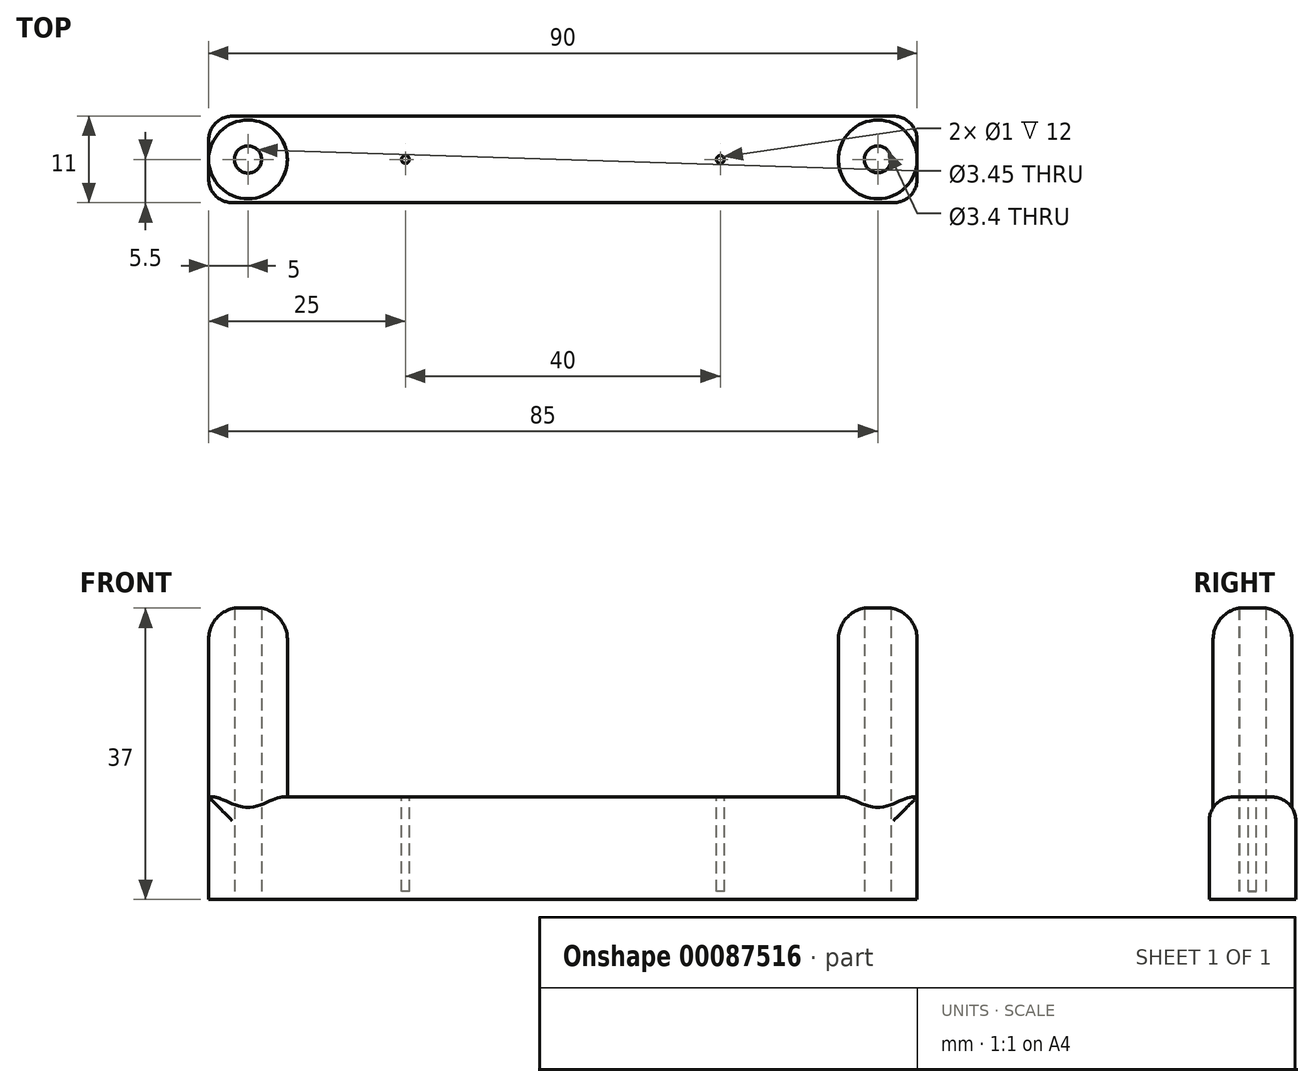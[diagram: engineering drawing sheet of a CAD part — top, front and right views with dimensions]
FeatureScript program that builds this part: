
annotation { "Feature Type Name" : "Feature", "Feature Type Description" : "" }
export const myFeature = defineFeature(function(context is Context, id is Id, definition is map)
    precondition{}
    {
        {
            var Q0;
            Q0=qCreatedBy(makeId("Top.planeOp"),FACE);
            var sketch = newSketch(context, id + "F0", { "sketchPlane" : qUnion([Q0])});
            skLineSegment(sketch, "E0.bottom", {"start": v(45, -5.5) * mm, "end": v(-45, -5.5) * mm});
            skLineSegment(sketch, "E0.top", {"start": v(45, 5.5) * mm, "end": v(-45, 5.5) * mm});
            skLineSegment(sketch, "E0.left", {"start": v(45, -5.5) * mm, "end": v(45, 5.5) * mm});
            skLineSegment(sketch, "E0.right", {"start": v(-45, -5.5) * mm, "end": v(-45, 5.5) * mm});
            skCircle(sketch, "E1", {"center": v(-40, 0) * mm, "radius": 1.73 * mm});
            skCircle(sketch, "E2", {"center": v(40, 0) * mm, "radius": 1.7 * mm});
            skSolve(sketch);
        }
        {
            var Q0;
            Q0=makeQuery(id+"F0.imprint","IMPRINT",FACE,{"disambiguationData":[TD([[makeQuery(id+"F0.imprint","IMPRINT",EDGE,{"derivedFrom":sQuery(id+"F0.wireOp",EDGE,"E0.bottom")}),-1.0]])]});
            var Q1;
            Q1=makeQuery(id+"F0.imprint","IMPRINT",FACE,{"disambiguationData":[TD([[makeQuery(id+"F0.imprint","IMPRINT",EDGE,{"derivedFrom":sQuery(id+"F0.wireOp",EDGE,"79vgDt6U-RJey-WxaV-HGEM-l305grDqS5GU")}),1.0]])]});
            extrude(context, id + "F1", {"entities" : qUnion([Q0, Q1]), "depth" : 13 * mm});
        }
        {
            var Q0;
            Q0=makeQuery(id+"F1.opExtrude","CAP_FACE",FACE,{"disambiguationData":[OSD([sQuery(id+"F0.wireOp",EDGE,"E0.bottom"),sQuery(id+"F0.wireOp",EDGE,"E0.top"),sQuery(id+"F0.wireOp",EDGE,"E0.left"),sQuery(id+"F0.wireOp",EDGE,"E0.right"),sQuery(id+"F0.wireOp",EDGE,"E1"),sQuery(id+"F0.wireOp",EDGE,"E2")])],"isStart":false});
            var sketch = newSketch(context, id + "F2", { "sketchPlane" : qUnion([Q0])});
            skCircle(sketch, "E3", {"center": v(40, 0) * mm, "radius": 5 * mm});
            skSolve(sketch);
        }
        {
            var Q0;
            Q0=makeQuery(id+"F2.imprint","IMPRINT",FACE,{"disambiguationData":[TD([[makeQuery(id+"F2.imprint","IMPRINT",EDGE,{"derivedFrom":sQuery(id+"F2.wireOp",EDGE,"E3")}),1.0]])]});
            extrude(context, id + "F3", {"entities" : qUnion([Q0]), "operationType" : NewBodyOperationType.ADD, "depth" : 24 * mm});
        }
        {
            var Q0;
            Q0=makeQuery(id+"F1.opExtrude","CAP_FACE",FACE,{"disambiguationData":[OSD([sQuery(id+"F0.wireOp",EDGE,"E0.bottom"),sQuery(id+"F0.wireOp",EDGE,"E0.top"),sQuery(id+"F0.wireOp",EDGE,"E0.left"),sQuery(id+"F0.wireOp",EDGE,"E0.right"),sQuery(id+"F0.wireOp",EDGE,"E1"),sQuery(id+"F0.wireOp",EDGE,"E2")])],"isStart":false});
            var sketch = newSketch(context, id + "F4", { "sketchPlane" : qUnion([Q0])});
            skCircle(sketch, "E4", {"center": v(-40, 0) * mm, "radius": 5 * mm});
            skSolve(sketch);
        }
        {
            var Q0;
            Q0=makeQuery(id+"F4.imprint","IMPRINT",FACE,{"disambiguationData":[TD([[makeQuery(id+"F4.imprint","IMPRINT",EDGE,{"derivedFrom":sQuery(id+"F4.wireOp",EDGE,"E4")}),1.0]])]});
            extrude(context, id + "F5", {"entities" : qUnion([Q0]), "operationType" : NewBodyOperationType.ADD, "depth" : 24 * mm});
        }
        {
            var Q0;
            {var subQ2=sQuery(id+"F2.wireOp",EDGE,"E3");Q0=makeQuery(id+"F2.imprint","IMPRINT",FACE,{"disambiguationData":[TD([[makeQuery(id+"F2.imprint","IMPRINT",EDGE,{"derivedFrom":subQ2}),-1.0]])]});}
            var sketch = newSketch(context, id + "F6", { "sketchPlane" : qUnion([Q0])});
            skCircle(sketch, "E5", {"center": v(-20, 0) * mm, "radius": 0.5 * mm});
            skCircle(sketch, "E6", {"center": v(20, 0) * mm, "radius": 0.5 * mm});
            skSolve(sketch);
        }
        {
            var Q0;
            Q0=qSketchRegion(id+"F6",true);
            extrude(context, id + "F7", {"entities" : qUnion([Q0]), "operationType" : NewBodyOperationType.REMOVE, "oppositeDirection" : true, "depth" : 12 * mm});
        }
        {
            var Q0;
            Q0=makeQuery(id+"F1.opExtrude","CAP_EDGE",EDGE,{"disambiguationData":[OSD([sQuery(id+"F0.wireOp",EDGE,"E0.bottom")])],"isStart":false});
            var Q1;
            Q1=makeQuery(id+"F1.opExtrude","SWEPT_EDGE",EDGE,{"disambiguationData":[OSD([sQuery(id+"F0.wireOp",EDGE,"E0.bottom"),sQuery(id+"F0.wireOp",EDGE,"E0.right")])]});
            var Q2;
            Q2=makeQuery(id+"F1.opExtrude","SWEPT_EDGE",EDGE,{"disambiguationData":[OSD([sQuery(id+"F0.wireOp",EDGE,"E0.top"),sQuery(id+"F0.wireOp",EDGE,"E0.right")])]});
            var Q3;
            Q3=makeQuery(id+"F1.opExtrude","CAP_EDGE",EDGE,{"disambiguationData":[OSD([sQuery(id+"F0.wireOp",EDGE,"E0.top")])],"isStart":false});
            var Q4;
            Q4=makeQuery(id+"F1.opExtrude","SWEPT_EDGE",EDGE,{"disambiguationData":[OSD([sQuery(id+"F0.wireOp",EDGE,"E0.bottom"),sQuery(id+"F0.wireOp",EDGE,"E0.left")])]});
            var Q5;
            Q5=makeQuery(id+"F1.opExtrude","SWEPT_EDGE",EDGE,{"disambiguationData":[OSD([sQuery(id+"F0.wireOp",EDGE,"E0.top"),sQuery(id+"F0.wireOp",EDGE,"E0.left")])]});
            fillet(context, id + "F8", {"entities" : qUnion([Q0, Q1, Q2, Q3, Q4, Q5]), "radius" : 3 * mm, "tangentPropagation" : true, "allowEdgeOverflow" : false});
        }
        {
            var Q0;
            Q0=makeQuery(id+"F5.opExtrude","CAP_EDGE",EDGE,{"disambiguationData":[OSD([sQuery(id+"F4.wireOp",EDGE,"E4")])],"isStart":false});
            var Q1;
            Q1=makeQuery(id+"F3.opExtrude","CAP_EDGE",EDGE,{"disambiguationData":[OSD([sQuery(id+"F2.wireOp",EDGE,"E3")])],"isStart":false});
            fillet(context, id + "F9", {"entities" : qUnion([Q0, Q1]), "radius" : 4 * mm, "tangentPropagation" : true, "allowEdgeOverflow" : false});
        }
    });
